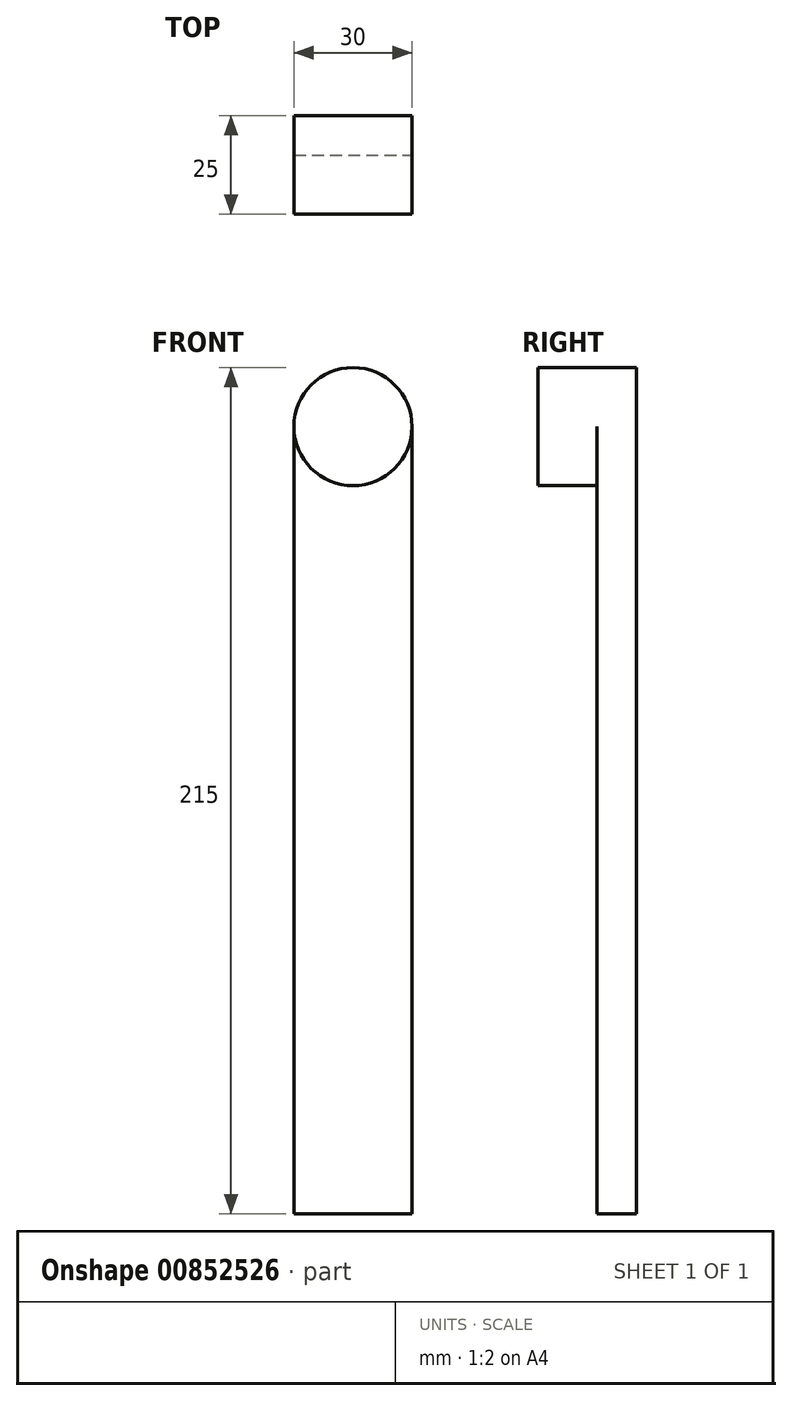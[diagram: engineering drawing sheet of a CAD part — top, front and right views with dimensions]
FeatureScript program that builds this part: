
annotation { "Feature Type Name" : "Feature", "Feature Type Description" : "" }
export const myFeature = defineFeature(function(context is Context, id is Id, definition is map)
    precondition{}
    {
        {
            var Q0;
            Q0=qCreatedBy(makeId("Front.planeOp"),FACE);
            var sketch = newSketch(context, id + "F0", { "sketchPlane" : qUnion([Q0])});
            skLineSegment(sketch, "E0.bottom", {"start": v(-15, 150) * mm, "end": v(15, 150) * mm});
            skLineSegment(sketch, "E0.top", {"start": v(-15, -50) * mm, "end": v(15, -50) * mm});
            skLineSegment(sketch, "E0.left", {"start": v(-15, 150) * mm, "end": v(-15, -50) * mm});
            skLineSegment(sketch, "E0.right", {"start": v(15, 150) * mm, "end": v(15, -50) * mm});
            skCircle(sketch, "E1", {"center": v(0, 150) * mm, "radius": 15 * mm});
            skPoint(sketch, "E1.centerSnap0", {"position": v(0, 150) * mm});
            skSolve(sketch);
        }
        {
            var Q0;
            {var subQ0=sQuery(id+"F0.wireOp",EDGE,"E0.bottom");Q0=makeQuery(id+"F0.imprint","IMPRINT",FACE,{"disambiguationData":[TD([[makeQuery(id+"F0.imprint","IMPRINT",EDGE,{"derivedFrom":subQ0}),1.0]])]});}
            var Q1;
            {var subQ0=sQuery(id+"F0.wireOp",EDGE,"E0.bottom");Q1=makeQuery(id+"F0.imprint","IMPRINT",FACE,{"disambiguationData":[TD([[makeQuery(id+"F0.imprint","IMPRINT",EDGE,{"derivedFrom":subQ0}),-1.0]])]});}
            extrude(context, id + "F1", {"entities" : qUnion([Q0, Q1]), "depth" : 25 * mm, "offsetDistance" : 25 * mm});
        }
        {
            var Q0;
            Q0 = qSketchRegion(id + "F0", true);
            extrude(context, id + "F2", {"entities" : qUnion([Q0]), "operationType" : NewBodyOperationType.ADD, "depth" : 10 * mm, "offsetDistance" : 25 * mm});
        }
    });
